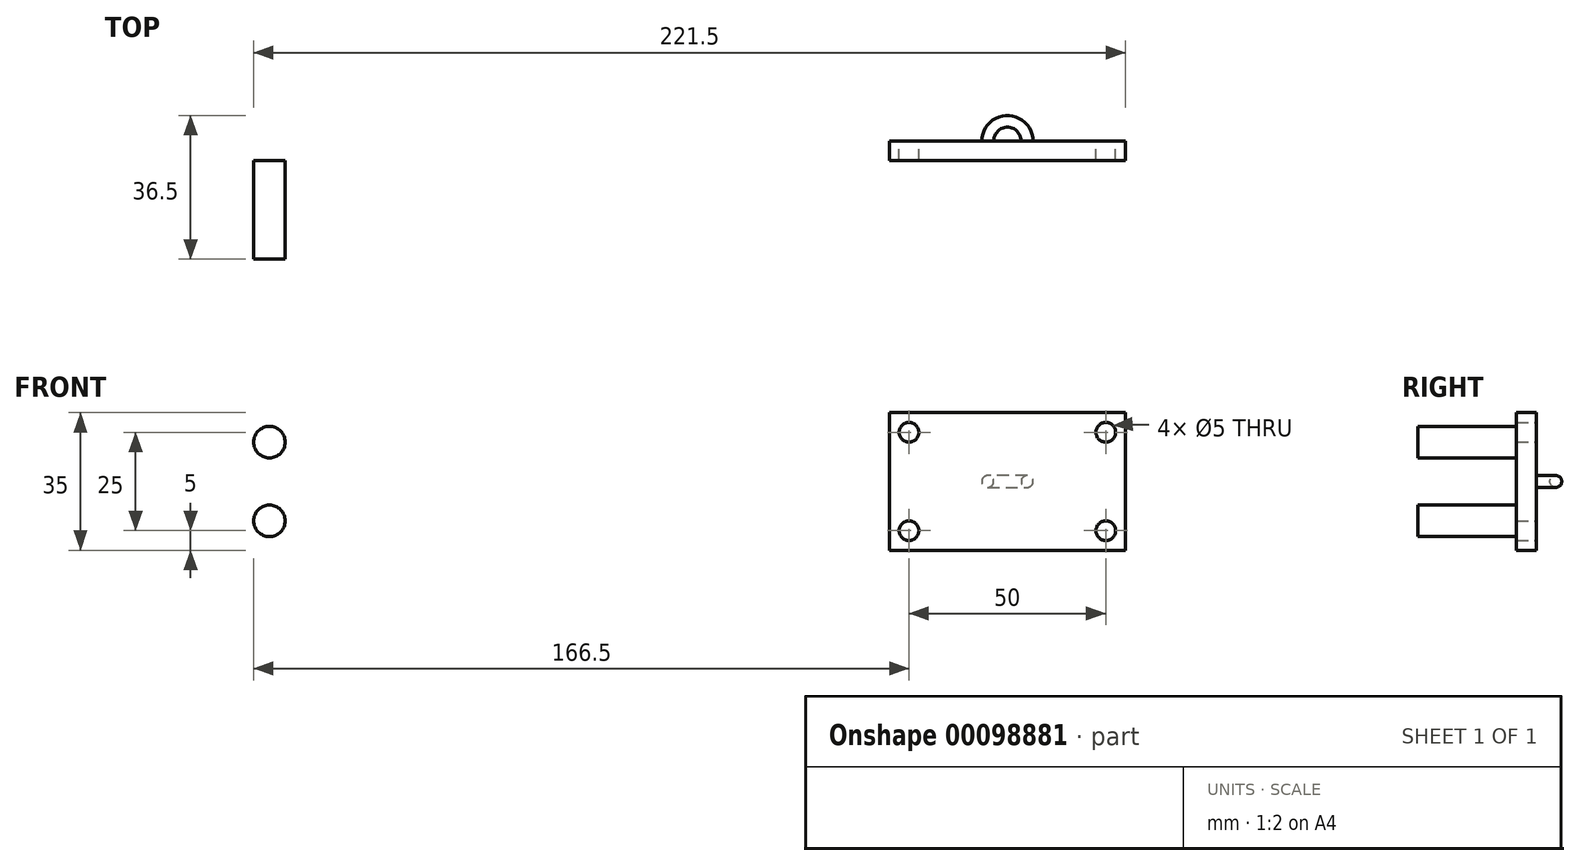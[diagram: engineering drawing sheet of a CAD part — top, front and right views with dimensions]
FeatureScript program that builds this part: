
annotation { "Feature Type Name" : "Feature", "Feature Type Description" : "" }
export const myFeature = defineFeature(function(context is Context, id is Id, definition is map)
    precondition{}
    {
        {
            var Q0;
            Q0=qCreatedBy(makeId("Front.planeOp"),FACE);
            var sketch = newSketch(context, id + "F0", { "sketchPlane" : qUnion([Q0])});
            skLineSegment(sketch, "E0.bottom", {"start": v(200, 25) * mm, "end": v(-200, 25) * mm});
            skLineSegment(sketch, "E0.top", {"start": v(200, -25) * mm, "end": v(-200, -25) * mm});
            skLineSegment(sketch, "E0.left", {"start": v(200, 25) * mm, "end": v(200, -25) * mm});
            skLineSegment(sketch, "E0.right", {"start": v(-200, 25) * mm, "end": v(-200, -25) * mm});
            skPoint(sketch, "E0.middle", {"position": v(0, 0) * mm});
            skSolve(sketch);
        }
        {
            var Q0;
            Q0 = qSketchRegion(id + "F0", true);
            extrude(context, id + "F1", {"entities" : qUnion([Q0]), "depth" : 25 * mm});
        }
        {
            var Q0;
            Q0=makeQuery(id+"F1.opExtrude","CAP_FACE",FACE,{"disambiguationData":[OSD([sQuery(id+"F0.wireOp",EDGE,"E0.bottom"),sQuery(id+"F0.wireOp",EDGE,"E0.top"),sQuery(id+"F0.wireOp",EDGE,"E0.left"),sQuery(id+"F0.wireOp",EDGE,"E0.right")])],"isStart":false});
            var sketch = newSketch(context, id + "F2", { "sketchPlane" : qUnion([Q0])});
            skCircle(sketch, "E1", {"center": v(187.5, -10) * mm, "radius": 4 * mm});
            skCircle(sketch, "E2", {"center": v(187.5, 10) * mm, "radius": 4 * mm});
            skCircle(sketch, "E3.MirrorC", {"center": v(-187.5, 10) * mm, "radius": 4 * mm});
            skCircle(sketch, "E4.MirrorC", {"center": v(-187.5, -10) * mm, "radius": 4 * mm});
            skSolve(sketch);
        }
        {
            var Q0;
            Q0=makeQuery(id+"F2.imprint","IMPRINT",FACE,{"disambiguationData":[TD([[makeQuery(id+"F2.imprint","IMPRINT",EDGE,{"derivedFrom":sQuery(id+"F2.wireOp",EDGE,"E3.MirrorC")}),-1.0]])]});
            var Q1;
            Q1=makeQuery(id+"F2.imprint","IMPRINT",FACE,{"disambiguationData":[TD([[makeQuery(id+"F2.imprint","IMPRINT",EDGE,{"derivedFrom":sQuery(id+"F2.wireOp",EDGE,"E4.MirrorC")}),-1.0]])]});
            var Q2;
            Q2=makeQuery(id+"F2.imprint","IMPRINT",FACE,{"disambiguationData":[TD([[makeQuery(id+"F2.imprint","IMPRINT",EDGE,{"derivedFrom":sQuery(id+"F2.wireOp",EDGE,"E2")}),1.0]])]});
            var Q3;
            Q3=makeQuery(id+"F2.imprint","IMPRINT",FACE,{"disambiguationData":[TD([[makeQuery(id+"F2.imprint","IMPRINT",EDGE,{"derivedFrom":sQuery(id+"F2.wireOp",EDGE,"E1")}),1.0]])]});
            extrude(context, id + "F3", {"entities" : qUnion([Q0, Q1, Q2, Q3]), "operationType" : NewBodyOperationType.REMOVE, "endBound" : BoundingType.UP_TO_NEXT, "oppositeDirection" : true, "depth" : 25 * mm});
        }
        {
            var Q0;
            Q0=makeQuery(id+"F1.opExtrude","CAP_FACE",FACE,{"disambiguationData":[OSD([sQuery(id+"F0.wireOp",EDGE,"E0.bottom"),sQuery(id+"F0.wireOp",EDGE,"E0.top"),sQuery(id+"F0.wireOp",EDGE,"E0.left"),sQuery(id+"F0.wireOp",EDGE,"E0.right")])],"isStart":true});
            var sketch = newSketch(context, id + "F4", { "sketchPlane" : qUnion([Q0])});
            skLineSegment(sketch, "E5.bottom", {"start": v(30, 17.5) * mm, "end": v(-30, 17.5) * mm});
            skLineSegment(sketch, "E5.top", {"start": v(30, -17.5) * mm, "end": v(-30, -17.5) * mm});
            skLineSegment(sketch, "E5.left", {"start": v(30, 17.5) * mm, "end": v(30, -17.5) * mm});
            skLineSegment(sketch, "E5.right", {"start": v(-30, 17.5) * mm, "end": v(-30, -17.5) * mm});
            skPoint(sketch, "E5.middle", {"position": v(0, 0) * mm});
            skSolve(sketch);
        }
        {
            var Q0;
            Q0 = qSketchRegion(id + "F4", true);
            extrude(context, id + "F5", {"entities" : qUnion([Q0]), "operationType" : NewBodyOperationType.ADD, "depth" : 5 * mm});
        }
        {
            var Q0;
            Q0=makeQuery(id+"F5.opExtrude","CAP_FACE",FACE,{"disambiguationData":[OSD([sQuery(id+"F4.wireOp",EDGE,"E5.bottom"),sQuery(id+"F4.wireOp",EDGE,"E5.top"),sQuery(id+"F4.wireOp",EDGE,"E5.left"),sQuery(id+"F4.wireOp",EDGE,"E5.right")])],"isStart":false});
            var sketch = newSketch(context, id + "F6", { "sketchPlane" : qUnion([Q0])});
            skPoint(sketch, "E6.middle", {"position": v(0, 0) * mm});
            skCircle(sketch, "E7", {"center": v(-25, 12.5) * mm, "radius": 2.5 * mm});
            skCircle(sketch, "E8", {"center": v(-25, -12.5) * mm, "radius": 2.5 * mm});
            skCircle(sketch, "E9", {"center": v(25, -12.5) * mm, "radius": 2.5 * mm});
            skCircle(sketch, "E10", {"center": v(25, 12.5) * mm, "radius": 2.5 * mm});
            skSolve(sketch);
        }
        {
            var Q0;
            Q0=makeQuery(id+"F6.imprint","IMPRINT",FACE,{"disambiguationData":[TD([[makeQuery(id+"F6.imprint","IMPRINT",EDGE,{"derivedFrom":sQuery(id+"F6.wireOp",EDGE,"E7")}),1.0]])]});
            var Q1;
            Q1=makeQuery(id+"F6.imprint","IMPRINT",FACE,{"disambiguationData":[TD([[makeQuery(id+"F6.imprint","IMPRINT",EDGE,{"derivedFrom":sQuery(id+"F6.wireOp",EDGE,"E10")}),1.0]])]});
            var Q2;
            Q2=makeQuery(id+"F6.imprint","IMPRINT",FACE,{"disambiguationData":[TD([[makeQuery(id+"F6.imprint","IMPRINT",EDGE,{"derivedFrom":sQuery(id+"F6.wireOp",EDGE,"E9")}),1.0]])]});
            var Q3;
            Q3=makeQuery(id+"F6.imprint","IMPRINT",FACE,{"disambiguationData":[TD([[makeQuery(id+"F6.imprint","IMPRINT",EDGE,{"derivedFrom":sQuery(id+"F6.wireOp",EDGE,"E8")}),1.0]])]});
            extrude(context, id + "F7", {"entities" : qUnion([Q0, Q1, Q2, Q3]), "operationType" : NewBodyOperationType.REMOVE, "endBound" : BoundingType.THROUGH_ALL, "oppositeDirection" : true, "depth" : 25 * mm});
        }
        {
            var Q0;
            Q0=makeQuery(id+"F5.opExtrude","CAP_FACE",FACE,{"disambiguationData":[OSD([sQuery(id+"F4.wireOp",EDGE,"E5.bottom"),sQuery(id+"F4.wireOp",EDGE,"E5.top"),sQuery(id+"F4.wireOp",EDGE,"E5.left"),sQuery(id+"F4.wireOp",EDGE,"E5.right")])],"isStart":false});
            var sketch = newSketch(context, id + "F8", { "sketchPlane" : qUnion([Q0])});
            skLineSegment(sketch, "E11", {"start": v(0, 0) * mm, "end": v(-5, 0) * mm});
            skCircle(sketch, "E12", {"center": v(-5, 0) * mm, "radius": 1.5 * mm});
            skSolve(sketch);
        }
        {
            var Q0;
            Q0=sQuery(id+"F8.wireOp",VERTEX,"E12.center");
            var Q1;
            Q1=qCreatedBy(makeId("Top.planeOp"),FACE);
            cPlane(context, id + "F9", {"entities" : qUnion([Q0, Q1]), "cplaneType" : CPlaneType.PLANE_POINT, "offset" : 150 * mm, "width" : 150 * mm, "height" : 150 * mm});
        }
        {
            var Q0;
            Q0=qCreatedBy(id+"F9.planeOp",FACE);
            var sketch = newSketch(context, id + "F10", { "sketchPlane" : qUnion([Q0])});
            skLineSegment(sketch, "E13", {"start": v(0, 0) * mm, "end": v(0, 5) * mm});
            skArc(sketch, "E14", {"start": v(5, 5) * mm, "mid": v(0, 10) * mm, "end": v(-5, 5) * mm});
            skSolve(sketch);
        }
        {
            var Q0;
            Q0=makeQuery(id+"F8.imprint","IMPRINT",FACE,{"disambiguationData":[TD([[makeQuery(id+"F8.imprint","IMPRINT",EDGE,{"derivedFrom":sQuery(id+"F8.wireOp",EDGE,"E12")}),1.0]])]});
            var Q1;
            Q1=sQuery(id+"F8.wireOp",EDGE,"E12");
            var Q2;
            Q2=sQuery(id+"F10.wireOp",EDGE,"E14");
            sweep(context, id + "F11", {"operationType" : NewBodyOperationType.ADD, "profiles" : qUnion([Q0]), "surfaceProfiles" : qUnion([Q1]), "path" : qUnion([Q2])});
        }
    });
